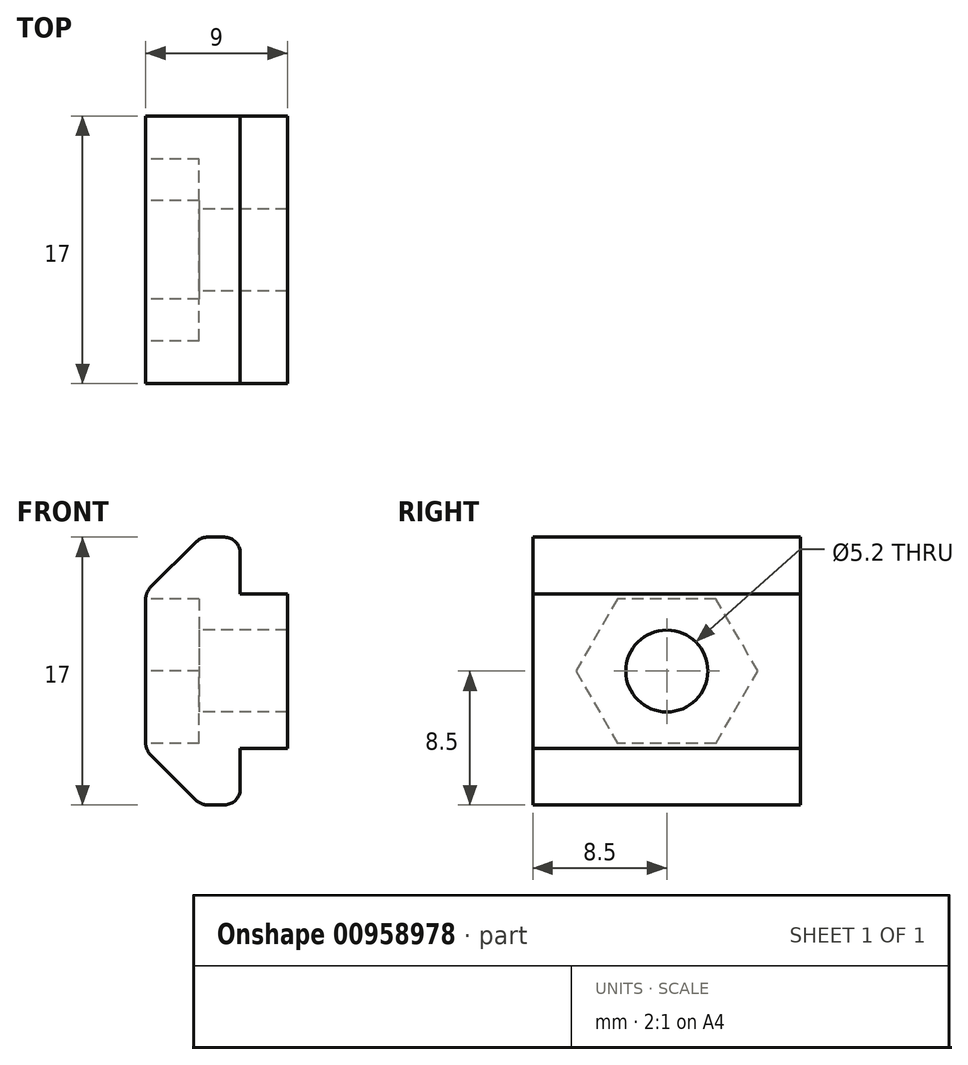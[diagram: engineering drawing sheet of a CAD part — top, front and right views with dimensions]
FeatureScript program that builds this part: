
annotation { "Feature Type Name" : "Feature", "Feature Type Description" : "" }
export const myFeature = defineFeature(function(context is Context, id is Id, definition is map)
    precondition{}
    {
        {
            var Q0;
            Q0=qCreatedBy(makeId("Front.planeOp"),FACE);
            var sketch = newSketch(context, id + "F0", { "sketchPlane" : qUnion([Q0])});
            skLineSegment(sketch, "E0", {"start": v(-8.18, -2.7) * mm, "end": v(-0.27, -2.7) * mm, "construction": true});
            skLineSegment(sketch, "E1", {"start": v(-0.27, 2.2) * mm, "end": v(-8.18, 2.2) * mm, "construction": true});
            skLineSegment(sketch, "E2", {"start": v(-0.27, -2.7) * mm, "end": v(0.27, -3.25) * mm, "construction": true});
            skLineSegment(sketch, "E3", {"start": v(0.27, 2.75) * mm, "end": v(-0.27, 2.2) * mm, "construction": true});
            skLineSegment(sketch, "E4", {"start": v(-0.27, 2.2) * mm, "end": v(-0.27, -2.7) * mm, "construction": true});
            skLineSegment(sketch, "E5", {"start": v(-8.18, 2.2) * mm, "end": v(-8.73, 2.75) * mm, "construction": true});
            skLineSegment(sketch, "E6", {"start": v(-8.73, -3.25) * mm, "end": v(-8.18, -2.7) * mm, "construction": true});
            skLineSegment(sketch, "E7", {"start": v(-8.18, 2.2) * mm, "end": v(-8.18, -2.7) * mm, "construction": true});
            skLineSegment(sketch, "E8", {"start": v(-8.73, 2.75) * mm, "end": v(0.27, 2.75) * mm, "construction": true});
            skLineSegment(sketch, "E9", {"start": v(-8.73, -3.25) * mm, "end": v(0.27, -3.25) * mm, "construction": true});
            skLineSegment(sketch, "E10", {"start": v(-9.18, -0.25) * mm, "end": v(0.72, -0.25) * mm, "construction": true});
            skLineSegment(sketch, "E11", {"start": v(-8.73, 4.34) * mm, "end": v(-8.73, -4.84) * mm});
            skArc(sketch, "E12", {"start": v(-8.73, -4.84) * mm, "mid": v(-8.65, -5.22) * mm, "end": v(-8.43, -5.54) * mm});
            skLineSegment(sketch, "E13", {"start": v(-8.43, -5.54) * mm, "end": v(-5.52, -8.46) * mm});
            skArc(sketch, "E14", {"start": v(-5.52, -8.46) * mm, "mid": v(-5.2, -8.67) * mm, "end": v(-4.81, -8.75) * mm});
            skLineSegment(sketch, "E15", {"start": v(-4.81, -8.75) * mm, "end": v(-3.73, -8.75) * mm});
            skArc(sketch, "E16", {"start": v(-3.73, -8.75) * mm, "mid": v(-3.02, -8.46) * mm, "end": v(-2.73, -7.75) * mm});
            skLineSegment(sketch, "E17", {"start": v(-2.73, -7.75) * mm, "end": v(-2.73, -5.15) * mm});
            skLineSegment(sketch, "E18", {"start": v(-2.73, -5.15) * mm, "end": v(0.27, -5.15) * mm});
            skLineSegment(sketch, "E19", {"start": v(0.27, -5.15) * mm, "end": v(0.27, 4.65) * mm});
            skLineSegment(sketch, "E20", {"start": v(0.27, 4.65) * mm, "end": v(-2.73, 4.65) * mm});
            skLineSegment(sketch, "E21", {"start": v(-2.73, 4.65) * mm, "end": v(-2.73, 7.25) * mm});
            skArc(sketch, "E22", {"start": v(-2.73, 7.25) * mm, "mid": v(-3.02, 7.96) * mm, "end": v(-3.73, 8.25) * mm});
            skLineSegment(sketch, "E23", {"start": v(-3.73, 8.25) * mm, "end": v(-4.81, 8.25) * mm});
            skArc(sketch, "E24", {"start": v(-4.81, 8.25) * mm, "mid": v(-5.2, 8.17) * mm, "end": v(-5.52, 7.96) * mm});
            skLineSegment(sketch, "E25", {"start": v(-5.52, 7.96) * mm, "end": v(-8.43, 5.04) * mm});
            skArc(sketch, "E26", {"start": v(-8.43, 5.04) * mm, "mid": v(-8.65, 4.72) * mm, "end": v(-8.73, 4.34) * mm});
            skSolve(sketch);
        }
        {
            var Q0;
            Q0=makeQuery(id+"F0.imprint","IMPRINT",FACE,{"disambiguationData":[TD([[makeQuery(id+"F0.imprint","IMPRINT",EDGE,{"derivedFrom":sQuery(id+"F0.wireOp",EDGE,"E11")}),1.0]])]});
            extrude(context, id + "F1", {"entities" : qUnion([Q0]), "oppositeDirection" : true, "depth" : 17 * mm, "offsetDistance" : 25 * mm});
        }
        {
            var Q0;
            Q0=makeQuery(id+"F1.opExtrude","SWEPT_FACE",FACE,{"disambiguationData":[OSD([sQuery(id+"F0.wireOp",EDGE,"E11")])]});
            var sketch = newSketch(context, id + "F2", { "sketchPlane" : qUnion([Q0])});
            skLineSegment(sketch, "E27", {"start": v(0, -4.84) * mm, "end": v(-17, 4.34) * mm, "construction": true});
            skLineSegment(sketch, "E28", {"start": v(0, 4.34) * mm, "end": v(-17, -4.84) * mm, "construction": true});
            skPoint(sketch, "E29", {"position": v(-8.5, -0.25) * mm});
            skCircle(sketch, "E30.cCircle", {"center": v(-8.5, -0.25) * mm, "radius": 5 * mm, "construction": true});
            skLineSegment(sketch, "E30.0", {"start": v(-5.61, -5.25) * mm, "end": v(-11.39, -5.25) * mm});
            skLineSegment(sketch, "E30.1", {"start": v(-11.39, -5.25) * mm, "end": v(-14.27, -0.25) * mm});
            skLineSegment(sketch, "E30.2", {"start": v(-14.27, -0.25) * mm, "end": v(-11.39, 4.75) * mm});
            skLineSegment(sketch, "E30.3", {"start": v(-11.39, 4.75) * mm, "end": v(-5.61, 4.75) * mm});
            skLineSegment(sketch, "E30.4", {"start": v(-5.61, 4.75) * mm, "end": v(-2.73, -0.25) * mm});
            skLineSegment(sketch, "E30.5", {"start": v(-2.73, -0.25) * mm, "end": v(-5.61, -5.25) * mm});
            skPoint(sketch, "E30.0.midPoint", {"position": v(-8.5, -5.25) * mm});
            skCircle(sketch, "E31", {"center": v(-8.5, -0.25) * mm, "radius": 2.6 * mm});
            skSolve(sketch);
        }
        {
            var Q0;
            Q0=makeQuery(id+"F2.imprint","IMPRINT",FACE,{"disambiguationData":[TD([[makeQuery(id+"F2.imprint","IMPRINT",EDGE,{"derivedFrom":sQuery(id+"F2.wireOp",EDGE,"E31")}),-1.0]])]});
            var Q1;
            Q1=makeQuery(id+"F2.imprint","IMPRINT",FACE,{"disambiguationData":[TD([[makeQuery(id+"F2.imprint","IMPRINT",EDGE,{"derivedFrom":sQuery(id+"F2.wireOp",EDGE,"E31")}),1.0]])]});
            extrude(context, id + "F3", {"entities" : qUnion([Q0, Q1]), "operationType" : NewBodyOperationType.REMOVE, "oppositeDirection" : true, "depth" : 3.4 * mm, "offsetDistance" : 25 * mm});
        }
        {
            var Q0;
            Q0=makeQuery(id+"F2.imprint","IMPRINT",FACE,{"disambiguationData":[TD([[makeQuery(id+"F2.imprint","IMPRINT",EDGE,{"derivedFrom":sQuery(id+"F2.wireOp",EDGE,"E31")}),1.0]])]});
            extrude(context, id + "F4", {"entities" : qUnion([Q0]), "operationType" : NewBodyOperationType.REMOVE, "endBound" : BoundingType.THROUGH_ALL, "oppositeDirection" : true, "depth" : 25 * mm, "offsetDistance" : 25 * mm});
        }
    });
